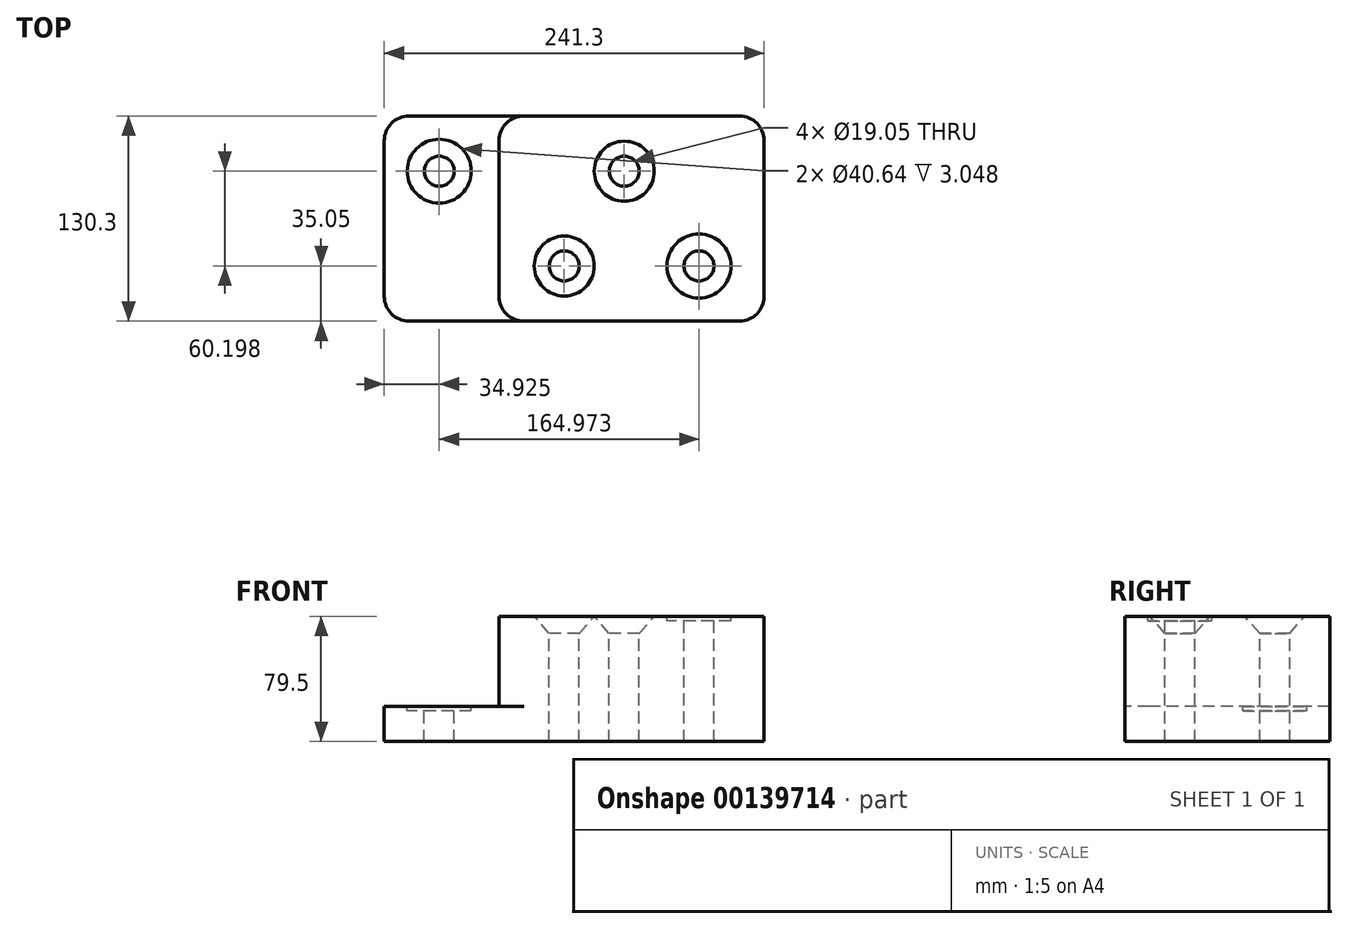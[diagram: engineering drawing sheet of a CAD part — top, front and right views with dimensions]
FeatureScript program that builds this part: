
annotation { "Feature Type Name" : "Feature", "Feature Type Description" : "" }
export const myFeature = defineFeature(function(context is Context, id is Id, definition is map)
    precondition{}
    {
        {
            var Q0;
            Q0=qCreatedBy(makeId("Top.planeOp"),FACE);
            var sketch = newSketch(context, id + "F0", { "sketchPlane" : qUnion([Q0])});
            skLineSegment(sketch, "E0", {"start": v(0, 0) * mm, "end": v(0, -130.3) * mm});
            skLineSegment(sketch, "E1", {"start": v(0, -130.3) * mm, "end": v(241.3, -130.3) * mm});
            skLineSegment(sketch, "E2", {"start": v(241.3, -130.3) * mm, "end": v(241.3, 0) * mm});
            skLineSegment(sketch, "E3", {"start": v(241.3, 0) * mm, "end": v(0, 0) * mm});
            skSolve(sketch);
        }
        {
            var Q0;
            Q0 = qSketchRegion(id + "F0", true);
            extrude(context, id + "F1", {"entities" : qUnion([Q0]), "depth" : 22.35 * mm});
        }
        {
            var Q0;
            Q0=makeQuery(id+"F1.opExtrude","SWEPT_EDGE",EDGE,{"disambiguationData":[OSD([sQuery(id+"F0.wireOp",EDGE,"E0"),sQuery(id+"F0.wireOp",EDGE,"E1")])]});
            var Q1;
            Q1=makeQuery(id+"F1.opExtrude","SWEPT_EDGE",EDGE,{"disambiguationData":[OSD([sQuery(id+"F0.wireOp",EDGE,"E1"),sQuery(id+"F0.wireOp",EDGE,"E2")])]});
            var Q2;
            Q2=makeQuery(id+"F1.opExtrude","SWEPT_EDGE",EDGE,{"disambiguationData":[OSD([sQuery(id+"F0.wireOp",EDGE,"E2"),sQuery(id+"F0.wireOp",EDGE,"E3")])]});
            var Q3;
            Q3=makeQuery(id+"F1.opExtrude","SWEPT_EDGE",EDGE,{"disambiguationData":[OSD([sQuery(id+"F0.wireOp",EDGE,"E0"),sQuery(id+"F0.wireOp",EDGE,"E3")])]});
            fillet(context, id + "F2", {"entities" : qUnion([Q0, Q1, Q2, Q3]), "radius" : 15.75 * mm, "tangentPropagation" : true, "allowEdgeOverflow" : false});
        }
        {
            var Q0;
            Q0=makeQuery(id+"F1.opExtrude","CAP_FACE",FACE,{"disambiguationData":[OSD([sQuery(id+"F0.wireOp",EDGE,"E0"),sQuery(id+"F0.wireOp",EDGE,"E1"),sQuery(id+"F0.wireOp",EDGE,"E2"),sQuery(id+"F0.wireOp",EDGE,"E3")])],"isStart":false});
            var sketch = newSketch(context, id + "F3", { "sketchPlane" : qUnion([Q0])});
            skLineSegment(sketch, "E4", {"start": v(72.9, 0) * mm, "end": v(72.9, -130.3) * mm});
            skLineSegment(sketch, "E5", {"start": v(72.9, -130.3) * mm, "end": v(241.3, -130.3) * mm});
            skLineSegment(sketch, "E6", {"start": v(241.3, -130.3) * mm, "end": v(241.3, 0) * mm});
            skLineSegment(sketch, "E7", {"start": v(241.3, 0) * mm, "end": v(72.9, 0) * mm});
            skSolve(sketch);
        }
        {
            var Q0;
            Q0 = qSketchRegion(id + "F3", true);
            extrude(context, id + "F4", {"entities" : qUnion([Q0]), "operationType" : NewBodyOperationType.ADD, "depth" : 57.15 * mm});
        }
        {
            var Q0;
            Q0=makeQuery(id+"F4.opExtrude","SWEPT_EDGE",EDGE,{"disambiguationData":[OSD([sQuery(id+"F3.wireOp",EDGE,"E5"),sQuery(id+"F3.wireOp",EDGE,"E6")])]});
            var Q1;
            Q1=makeQuery(id+"F4.opExtrude","SWEPT_EDGE",EDGE,{"disambiguationData":[OSD([sQuery(id+"F3.wireOp",EDGE,"E6"),sQuery(id+"F3.wireOp",EDGE,"E7")])]});
            var Q2;
            Q2=makeQuery(id+"F4.opExtrude","SWEPT_EDGE",EDGE,{"disambiguationData":[OSD([sQuery(id+"F0.wireOp",EDGE,"E1"),sQuery(id+"F3.wireOp",EDGE,"E4"),sQuery(id+"F3.wireOp",EDGE,"E5")])]});
            var Q3;
            Q3=makeQuery(id+"F4.opExtrude","SWEPT_EDGE",EDGE,{"disambiguationData":[OSD([sQuery(id+"F0.wireOp",EDGE,"E3"),sQuery(id+"F3.wireOp",EDGE,"E4"),sQuery(id+"F3.wireOp",EDGE,"E7")])]});
            fillet(context, id + "F5", {"entities" : qUnion([Q0, Q1, Q2, Q3]), "radius" : 15.75 * mm, "tangentPropagation" : true, "allowEdgeOverflow" : false});
        }
        {
            var Q0;
            Q0=makeQuery(id+"F4.opExtrude","CAP_FACE",FACE,{"disambiguationData":[OSD([sQuery(id+"F3.wireOp",EDGE,"E4"),sQuery(id+"F3.wireOp",EDGE,"E5"),sQuery(id+"F3.wireOp",EDGE,"E6"),sQuery(id+"F3.wireOp",EDGE,"E7")])],"isStart":false});
            var sketch = newSketch(context, id + "F6", { "sketchPlane" : qUnion([Q0])});
            skPoint(sketch, "E8", {"position": v(152.4, -35.05) * mm});
            skPoint(sketch, "E9", {"position": v(199.9, -95.25) * mm});
            skPoint(sketch, "E10", {"position": v(114.3, -95.25) * mm});
            skPoint(sketch, "E11", {"position": v(34.93, -35.05) * mm});
            skSolve(sketch);
        }
        {
            var Q0;
            Q0=sQuery(id+"F6.wireOp",VERTEX,"E10");
            var Q1;
            Q1=sQuery(id+"F6.wireOp",VERTEX,"E8");
            var Q2;
            Q2=makeQuery(id+"F1.opExtrude","SWEPT_BODY",BODY,{"disambiguationData":[OSD([sQuery(id+"F0.wireOp",EDGE,"E0"),sQuery(id+"F0.wireOp",EDGE,"E1"),sQuery(id+"F0.wireOp",EDGE,"E2"),sQuery(id+"F0.wireOp",EDGE,"E3")])]});
            hole(context, id + "F7", {"style" : HoleStyle.C_SINK, "endStyle" : HoleEndStyle.THROUGH, "holeDiameter" : 19.05 * mm, "cSinkDiameter" : 38.1 * mm, "cSinkAngle" : 82 * degree, "locations" : qUnion([Q0, Q1]), "scope" : qUnion([Q2]), "isTappedThrough" : true});
        }
        {
            var Q0;
            Q0=sQuery(id+"F6.wireOp",VERTEX,"E9");
            var Q1;
            Q1=sQuery(id+"F6.wireOp",VERTEX,"E11");
            var Q2;
            Q2=makeQuery(id+"F1.opExtrude","SWEPT_BODY",BODY,{"disambiguationData":[OSD([sQuery(id+"F0.wireOp",EDGE,"E0"),sQuery(id+"F0.wireOp",EDGE,"E1"),sQuery(id+"F0.wireOp",EDGE,"E2"),sQuery(id+"F0.wireOp",EDGE,"E3")])]});
            hole(context, id + "F8", {"style" : HoleStyle.C_BORE, "endStyle" : HoleEndStyle.THROUGH, "holeDiameter" : 19.05 * mm, "cBoreDiameter" : 40.64 * mm, "cBoreDepth" : 3.05 * mm, "locations" : qUnion([Q0, Q1]), "scope" : qUnion([Q2]), "isTappedThrough" : true});
        }
    });
